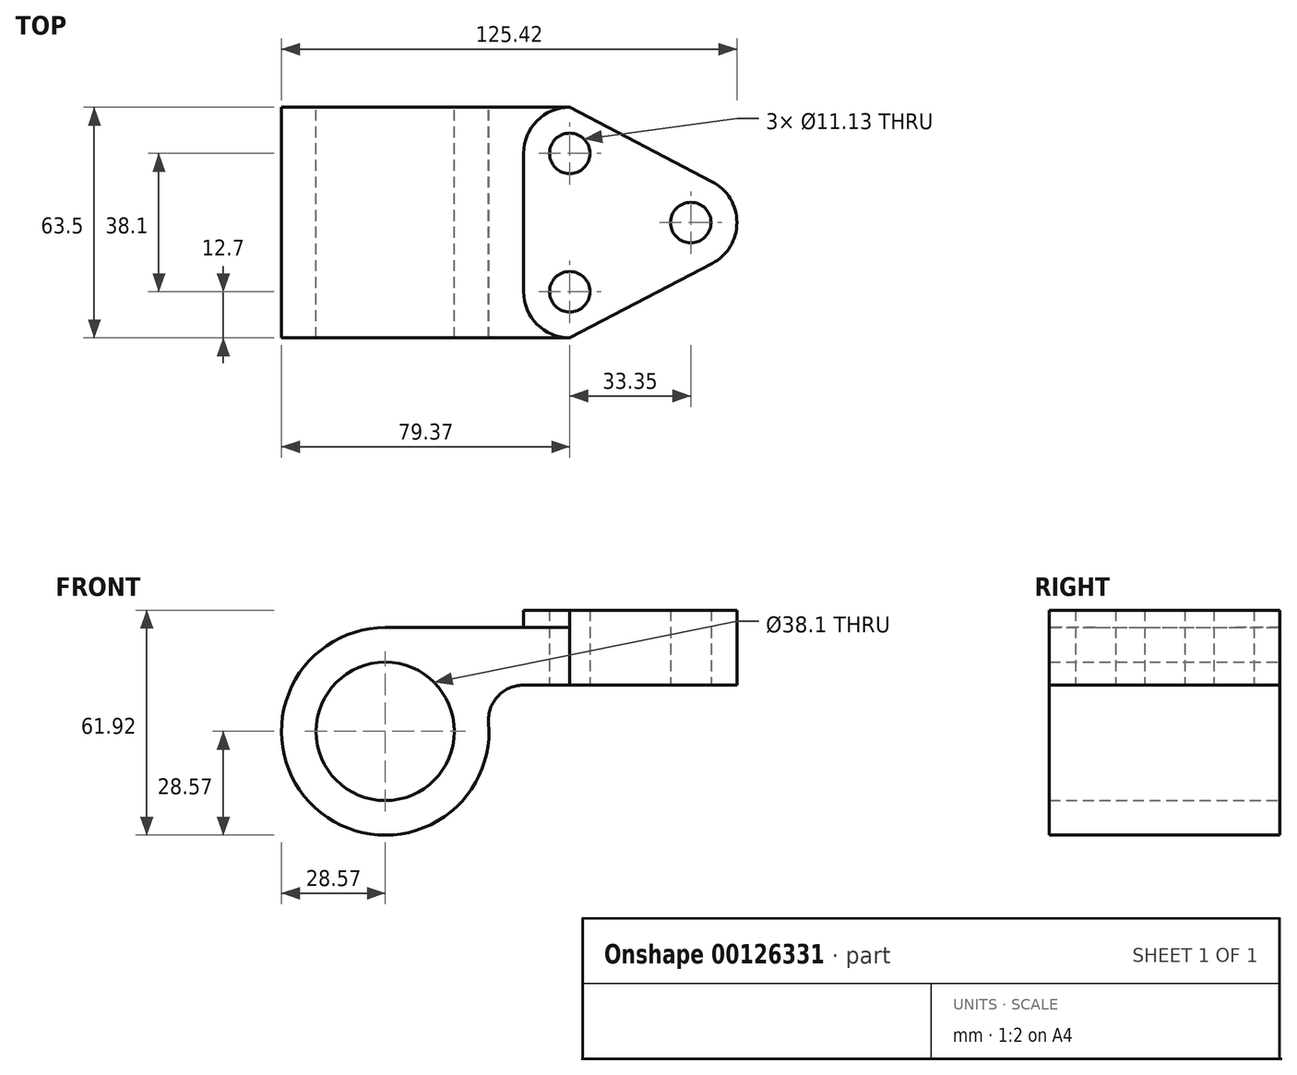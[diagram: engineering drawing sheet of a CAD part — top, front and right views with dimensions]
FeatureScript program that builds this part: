
annotation { "Feature Type Name" : "Feature", "Feature Type Description" : "" }
export const myFeature = defineFeature(function(context is Context, id is Id, definition is map)
    precondition{}
    {
        {
            var Q0;
            Q0=qCreatedBy(makeId("Front.planeOp"),FACE);
            var sketch = newSketch(context, id + "F0", { "sketchPlane" : qUnion([Q0])});
            skCircle(sketch, "E0", {"center": v(0, 0) * mm, "radius": 19.05 * mm});
            skCircle(sketch, "E1", {"center": v(0, 0) * mm, "radius": 28.58 * mm});
            skLineSegment(sketch, "E2", {"start": v(0, 28.58) * mm, "end": v(50.8, 28.58) * mm});
            skLineSegment(sketch, "E3", {"start": v(50.8, 28.58) * mm, "end": v(50.8, 12.7) * mm});
            skLineSegment(sketch, "E4", {"start": v(50.8, 12.7) * mm, "end": v(37.97, 12.7) * mm});
            skArc(sketch, "E5", {"start": v(37.97, 12.7) * mm, "mid": v(30.96, 9.62) * mm, "end": v(28.48, 2.38) * mm});
            skSolve(sketch);
        }
        {
            var Q0;
            {var subQ0=sQuery(id+"F0.wireOp",EDGE,"E2");Q0=makeQuery(id+"F0.imprint","IMPRINT",FACE,{"disambiguationData":[TD([[makeQuery(id+"F0.imprint","IMPRINT",EDGE,{"derivedFrom":subQ0}),-1.0]])]});}
            var Q1;
            Q1=makeQuery(id+"F0.imprint","IMPRINT",FACE,{"disambiguationData":[TD([[makeQuery(id+"F0.imprint","IMPRINT",EDGE,{"derivedFrom":sQuery(id+"F0.wireOp",EDGE,"E0")}),-1.0]])]});
            extrude(context, id + "F1", {"entities" : qUnion([Q0, Q1]), "depth" : 63.5 * mm});
        }
        {
            var Q0;
            Q0=makeQuery(id+"F1.opExtrude","SWEPT_FACE",FACE,{"disambiguationData":[OSD([sQuery(id+"F0.wireOp",EDGE,"E2")])]});
            var sketch = newSketch(context, id + "F2", { "sketchPlane" : qUnion([Q0])});
            skLineSegment(sketch, "E6", {"start": v(50.8, 0) * mm, "end": v(50.8, -12.7) * mm, "construction": true});
            skLineSegment(sketch, "E7", {"start": v(50.8, -12.7) * mm, "end": v(50.8, -50.8) * mm, "construction": true});
            skLineSegment(sketch, "E8", {"start": v(50.8, -50.8) * mm, "end": v(50.8, -63.5) * mm, "construction": true});
            skLineSegment(sketch, "E9", {"start": v(50.8, 0) * mm, "end": v(90.03, -20.5) * mm});
            skLineSegment(sketch, "E10", {"start": v(50.8, -63.5) * mm, "end": v(90.03, -43) * mm});
            skArc(sketch, "E11", {"start": v(90.03, -43) * mm, "mid": v(96.85, -31.75) * mm, "end": v(90.03, -20.5) * mm});
            skLineSegment(sketch, "E12", {"start": v(38.1, -12.7) * mm, "end": v(38.1, -50.8) * mm});
            skArc(sketch, "E13", {"start": v(50.8, 0) * mm, "mid": v(41.82, -3.72) * mm, "end": v(38.1, -12.7) * mm});
            skArc(sketch, "E14", {"start": v(38.1, -50.8) * mm, "mid": v(41.82, -59.78) * mm, "end": v(50.8, -63.5) * mm});
            skCircle(sketch, "E15", {"center": v(50.8, -12.7) * mm, "radius": 5.56 * mm});
            skCircle(sketch, "E16", {"center": v(50.8, -50.8) * mm, "radius": 5.56 * mm});
            skCircle(sketch, "E17", {"center": v(84.15, -31.75) * mm, "radius": 5.56 * mm});
            skSolve(sketch);
        }
        {
            var Q0;
            Q0 = qSketchRegion(id + "F2", true);
            extrude(context, id + "F3", {"entities" : qUnion([Q0]), "operationType" : NewBodyOperationType.ADD, "depth" : 4.78 * mm, "hasSecondDirection" : true, "secondDirectionOppositeDirection" : true, "secondDirectionDepth" : 15.88 * mm});
        }
        {
            var Q0;
            {var subQ0=sQuery(id+"F2.wireOp",EDGE,"E15");var subQ1=makeQuery(id+"F1.opExtrude","SWEPT_EDGE",EDGE,{"disambiguationData":[OSD([sQuery(id+"F0.wireOp",EDGE,"E2"),sQuery(id+"F0.wireOp",EDGE,"E3")])]});var subQ2=makeQuery(id+"F2.imprint","INTERSECT",VERTEX,{"disambiguationData":[OD(0.0)],"derivedFrom":[subQ1,subQ0]});Q0=makeQuery(id+"F2.imprint","IMPRINT",FACE,{"disambiguationData":[TD([[makeQuery(id+"F2.imprint","IMPRINT",EDGE,{"disambiguationData":[TD([[subQ2,-1.0]])],"derivedFrom":subQ0}),1.0]])]});}
            var Q1;
            {var subQ0=sQuery(id+"F2.wireOp",EDGE,"E16");var subQ1=makeQuery(id+"F1.opExtrude","SWEPT_EDGE",EDGE,{"disambiguationData":[OSD([sQuery(id+"F0.wireOp",EDGE,"E2"),sQuery(id+"F0.wireOp",EDGE,"E3")])]});var subQ2=makeQuery(id+"F2.imprint","INTERSECT",VERTEX,{"disambiguationData":[OD(0.0)],"derivedFrom":[subQ1,subQ0]});Q1=makeQuery(id+"F2.imprint","IMPRINT",FACE,{"disambiguationData":[TD([[makeQuery(id+"F2.imprint","IMPRINT",EDGE,{"disambiguationData":[TD([[subQ2,1.0]])],"derivedFrom":subQ0}),1.0]])]});}
            extrude(context, id + "F4", {"entities" : qUnion([Q0, Q1]), "operationType" : NewBodyOperationType.REMOVE, "endBound" : BoundingType.THROUGH_ALL, "oppositeDirection" : true, "depth" : 25.4 * mm});
        }
    });
